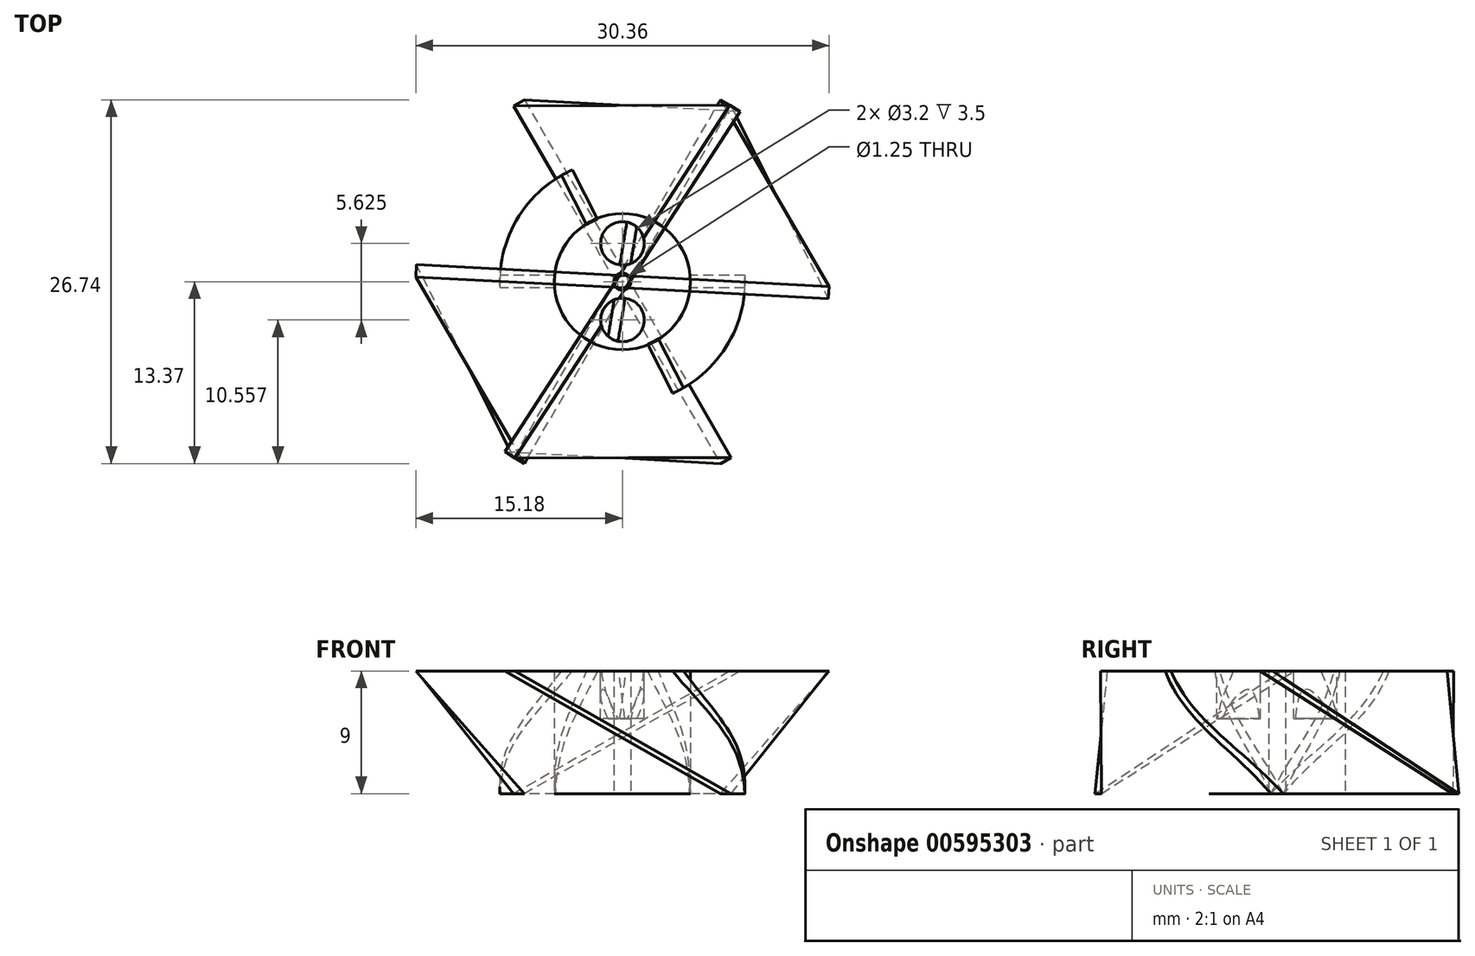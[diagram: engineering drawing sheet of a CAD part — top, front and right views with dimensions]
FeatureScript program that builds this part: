
annotation { "Feature Type Name" : "Feature", "Feature Type Description" : "" }
export const myFeature = defineFeature(function(context is Context, id is Id, definition is map)
    precondition{}
    {
        {
            var Q0;
            Q0=qCreatedBy(makeId("Top.planeOp"),FACE);
            cPlane(context, id + "F0", {"entities" : qUnion([Q0]), "cplaneType" : CPlaneType.OFFSET, "offset" : 9 * mm, "width" : 150 * mm, "height" : 150 * mm});
        }
        {
            var Q0;
            Q0=qCreatedBy(makeId("Top.planeOp"),FACE);
            cPlane(context, id + "F1", {"entities" : qUnion([Q0]), "cplaneType" : CPlaneType.OFFSET, "offset" : 3 * mm, "oppositeDirection" : true, "width" : 150 * mm, "height" : 150 * mm});
        }
        {
            var Q0;
            Q0=qCreatedBy(makeId("Top.planeOp"),FACE);
            var sketch = newSketch(context, id + "F2", { "sketchPlane" : qUnion([Q0])});
            skCircle(sketch, "E0", {"center": v(0, 0) * mm, "radius": 0.63 * mm});
            skCircle(sketch, "E1", {"center": v(0, 0) * mm, "radius": 5 * mm});
            skSolve(sketch);
        }
        {
            var Q0;
            Q0=qCreatedBy(id+"F0.planeOp",FACE);
            var sketch = newSketch(context, id + "F3", { "sketchPlane" : qUnion([Q0])});
            skCircle(sketch, "E2", {"center": v(0, 2.81) * mm, "radius": 1.6 * mm});
            skCircle(sketch, "E3", {"center": v(0, -2.81) * mm, "radius": 1.6 * mm});
            skSolve(sketch);
        }
        {
            var Q0;
            Q0=qCreatedBy(id+"F1.planeOp",FACE);
            var sketch = newSketch(context, id + "F4", { "sketchPlane" : qUnion([Q0])});
            skCircle(sketch, "E4", {"center": v(0, 0) * mm, "radius": 4.95 * mm});
            skCircle(sketch, "E5", {"center": v(0, 0) * mm, "radius": 9 * mm});
            skSolve(sketch);
        }
        {
            var Q0;
            Q0=qCreatedBy(makeId("Top.planeOp"),FACE);
            var sketch = newSketch(context, id + "F5", { "sketchPlane" : qUnion([Q0])});
            skLineSegment(sketch, "E6.bottom", {"start": v(15.18, -0.45) * mm, "end": v(-15.18, -0.45) * mm});
            skLineSegment(sketch, "E6.top", {"start": v(15.18, 0.45) * mm, "end": v(-15.18, 0.45) * mm});
            skLineSegment(sketch, "E6.left", {"start": v(15.18, -0.45) * mm, "end": v(15.18, 0.45) * mm});
            skLineSegment(sketch, "E6.right", {"start": v(-15.18, -0.45) * mm, "end": v(-15.18, 0.45) * mm});
            skPoint(sketch, "E6.middle", {"position": v(0, 0) * mm});
            skSolve(sketch);
        }
        {
            var Q0;
            Q0=qCreatedBy(makeId("Top.planeOp"),FACE);
            var sketch = newSketch(context, id + "F6", { "sketchPlane" : qUnion([Q0])});
            skPoint(sketch, "E7.middle", {"position": v(0, 0) * mm});
            skLineSegment(sketch, "E8.1.0", {"start": v(-7.2, 13.37) * mm, "end": v(7.98, -12.92) * mm});
            skLineSegment(sketch, "E8.1.1", {"start": v(-7.98, 12.92) * mm, "end": v(7.2, -13.37) * mm});
            skLineSegment(sketch, "E8.1.2", {"start": v(-7.2, 13.37) * mm, "end": v(-7.98, 12.92) * mm});
            skLineSegment(sketch, "E8.1.3", {"start": v(7.98, -12.92) * mm, "end": v(7.2, -13.37) * mm});
            skSolve(sketch);
        }
        {
            var Q0;
            Q0=qCreatedBy(makeId("Top.planeOp"),FACE);
            var sketch = newSketch(context, id + "F7", { "sketchPlane" : qUnion([Q0])});
            skPoint(sketch, "E9.middle", {"position": v(0, 0) * mm});
            skLineSegment(sketch, "E10.2.0", {"start": v(-7.98, -12.92) * mm, "end": v(7.2, 13.37) * mm});
            skLineSegment(sketch, "E10.2.1", {"start": v(-7.2, -13.37) * mm, "end": v(7.98, 12.92) * mm});
            skLineSegment(sketch, "E10.2.2", {"start": v(-7.98, -12.92) * mm, "end": v(-7.2, -13.37) * mm});
            skLineSegment(sketch, "E10.2.3", {"start": v(7.2, 13.37) * mm, "end": v(7.98, 12.92) * mm});
            skSolve(sketch);
        }
        {
            var Q0;
            Q0=qCreatedBy(id+"F0.planeOp",FACE);
            var sketch = newSketch(context, id + "F8", { "sketchPlane" : qUnion([Q0])});
            skLineSegment(sketch, "E11.bottom", {"start": v(6.49, -13.73) * mm, "end": v(-7.3, 13.32) * mm});
            skLineSegment(sketch, "E11.top", {"start": v(7.3, -13.32) * mm, "end": v(-6.49, 13.73) * mm});
            skLineSegment(sketch, "E11.left", {"start": v(6.49, -13.73) * mm, "end": v(7.3, -13.32) * mm});
            skLineSegment(sketch, "E11.right", {"start": v(-7.3, 13.32) * mm, "end": v(-6.49, 13.73) * mm});
            skPoint(sketch, "E11.middle", {"position": v(0, 0) * mm});
            skSolve(sketch);
        }
        {
            var Q0;
            Q0=qCreatedBy(id+"F0.planeOp",FACE);
            var sketch = newSketch(context, id + "F9", { "sketchPlane" : qUnion([Q0])});
            skPoint(sketch, "E12.middle", {"position": v(0, 0) * mm});
            skLineSegment(sketch, "E13.1.0", {"start": v(8.64, 12.48) * mm, "end": v(-7.89, -12.97) * mm});
            skLineSegment(sketch, "E13.1.1", {"start": v(7.89, 12.97) * mm, "end": v(-8.64, -12.48) * mm});
            skLineSegment(sketch, "E13.1.2", {"start": v(8.64, 12.48) * mm, "end": v(7.89, 12.97) * mm});
            skLineSegment(sketch, "E13.1.3", {"start": v(-7.89, -12.97) * mm, "end": v(-8.64, -12.48) * mm});
            skSolve(sketch);
        }
        {
            var Q0;
            Q0=qCreatedBy(id+"F0.planeOp",FACE);
            var sketch = newSketch(context, id + "F10", { "sketchPlane" : qUnion([Q0])});
            skPoint(sketch, "E14.middle", {"position": v(0, 0) * mm});
            skLineSegment(sketch, "E15.2.0", {"start": v(-15.13, 1.24) * mm, "end": v(15.18, -0.34) * mm});
            skLineSegment(sketch, "E15.2.1", {"start": v(-15.18, 0.34) * mm, "end": v(15.13, -1.24) * mm});
            skLineSegment(sketch, "E15.2.2", {"start": v(-15.13, 1.24) * mm, "end": v(-15.18, 0.34) * mm});
            skLineSegment(sketch, "E15.2.3", {"start": v(15.18, -0.34) * mm, "end": v(15.13, -1.24) * mm});
            skSolve(sketch);
        }
        {
            var Q0;
            Q0=makeQuery(id+"F5.imprint","IMPRINT",FACE,{"disambiguationData":[TD([[makeQuery(id+"F5.imprint","IMPRINT",EDGE,{"derivedFrom":sQuery(id+"F5.wireOp",EDGE,"E6.bottom")}),-1.0]])]});
            var Q1;
            Q1=makeQuery(id+"F8.imprint","IMPRINT",FACE,{"disambiguationData":[TD([[makeQuery(id+"F8.imprint","IMPRINT",EDGE,{"derivedFrom":sQuery(id+"F8.wireOp",EDGE,"E11.bottom")}),-1.0]])]});
            loft(context, id + "F11", {"sheetProfilesArray" : [{ "sheetProfileEntities" : qUnion([Q0]) }, { "sheetProfileEntities" : qUnion([Q1]) }]});
        }
        {
            var Q0;
            Q0=makeQuery(id+"F9.imprint","IMPRINT",FACE,{"disambiguationData":[TD([[makeQuery(id+"F9.imprint","IMPRINT",EDGE,{"derivedFrom":sQuery(id+"F9.wireOp",EDGE,"E13.1.0")}),-1.0]])]});
            var Q1;
            Q1=makeQuery(id+"F6.imprint","IMPRINT",FACE,{"disambiguationData":[TD([[makeQuery(id+"F6.imprint","IMPRINT",EDGE,{"derivedFrom":sQuery(id+"F6.wireOp",EDGE,"E8.1.0")}),-1.0]])]});
            loft(context, id + "F12", {"sheetProfilesArray" : [{ "sheetProfileEntities" : qUnion([Q0]) }, { "sheetProfileEntities" : qUnion([Q1]) }]});
        }
        {
            var Q0;
            Q0 = qSketchRegion(id + "F7", true);
            var Q1;
            Q1 = qSketchRegion(id + "F10", true);
            loft(context, id + "F13", {"sheetProfilesArray" : [{ "sheetProfileEntities" : qUnion([Q0]) }, { "sheetProfileEntities" : qUnion([Q1]) }]});
        }
        {
            var Q0;
            Q0=makeQuery(id+"F4.imprint","IMPRINT",FACE,{"disambiguationData":[TD([[makeQuery(id+"F4.imprint","IMPRINT",EDGE,{"derivedFrom":sQuery(id+"F4.wireOp",EDGE,"E4")}),-1.0]])]});
            extrude(context, id + "F14", {"entities" : qUnion([Q0]), "depth" : 25 * mm, "offsetDistance" : 25 * mm});
        }
        {
            var Q0;
            Q0=makeQuery(id+"F11.opLoft","SWEPT_BODY",BODY,{"disambiguationData":[OSD([makeQuery(id+"F5.imprint","IMPRINT",FACE,{"disambiguationData":[TD([[makeQuery(id+"F5.imprint","IMPRINT",EDGE,{"derivedFrom":sQuery(id+"F5.wireOp",EDGE,"E6.bottom")}),-1.0]])]}),makeQuery(id+"F8.imprint","IMPRINT",FACE,{"disambiguationData":[TD([[makeQuery(id+"F8.imprint","IMPRINT",EDGE,{"derivedFrom":sQuery(id+"F8.wireOp",EDGE,"E11.bottom")}),-1.0]])]})])]});
            var Q1;
            Q1=makeQuery(id+"F14.opExtrude","SWEPT_BODY",BODY,{"disambiguationData":[OSD([sQuery(id+"F4.wireOp",EDGE,"E4"),sQuery(id+"F4.wireOp",EDGE,"E5")])]});
            booleanBodies(context, id + "F15", {"operationType" : BooleanOperationType.INTERSECTION, "tools" : qUnion([Q0, Q1])});
        }
        {
            var Q0;
            Q0=makeQuery(id+"F2.imprint","IMPRINT",FACE,{"disambiguationData":[TD([[makeQuery(id+"F2.imprint","IMPRINT",EDGE,{"derivedFrom":sQuery(id+"F2.wireOp",EDGE,"E0")}),-1.0]])]});
            extrude(context, id + "F16", {"entities" : qUnion([Q0]), "depth" : 9 * mm, "offsetDistance" : 25 * mm});
        }
        {
            var Q0;
            Q0 = qSketchRegion(id + "F3", true);
            extrude(context, id + "F17", {"entities" : qUnion([Q0]), "operationType" : NewBodyOperationType.REMOVE, "oppositeDirection" : true, "depth" : 3.5 * mm, "offsetDistance" : 25 * mm});
        }
    });
